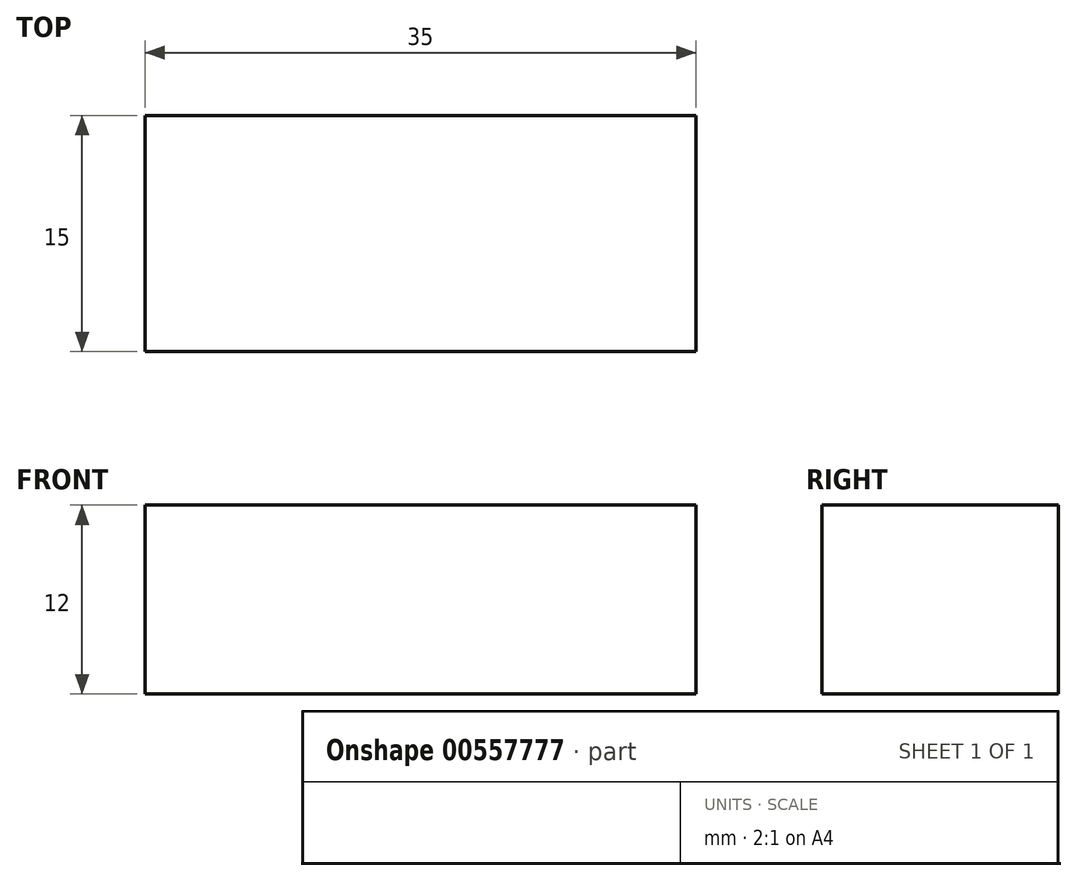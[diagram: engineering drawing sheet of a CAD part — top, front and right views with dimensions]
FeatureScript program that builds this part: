
annotation { "Feature Type Name" : "Feature", "Feature Type Description" : "" }
export const myFeature = defineFeature(function(context is Context, id is Id, definition is map)
    precondition{}
    {
        {
            var Q0;
            Q0=qCreatedBy(makeId("Top.planeOp"),FACE);
            var sketch = newSketch(context, id + "F0", { "sketchPlane" : qUnion([Q0])});
            skLineSegment(sketch, "E0.bottom", {"start": v(0, 0) * mm, "end": v(35, 0) * mm});
            skLineSegment(sketch, "E0.top", {"start": v(0, 15) * mm, "end": v(35, 15) * mm});
            skLineSegment(sketch, "E0.left", {"start": v(0, 0) * mm, "end": v(0, 15) * mm});
            skLineSegment(sketch, "E0.right", {"start": v(35, 0) * mm, "end": v(35, 15) * mm});
            skLineSegment(sketch, "E1", {"start": v(0, 7.5) * mm, "end": v(35, 7.5) * mm, "construction": true});
            skLineSegment(sketch, "E2", {"start": v(7.5, 15) * mm, "end": v(7.5, 0) * mm, "construction": true});
            skSolve(sketch);
        }
        {
            var Q0;
            Q0=makeQuery(id+"F0.imprint","IMPRINT",FACE,{"disambiguationData":[TD([[makeQuery(id+"F0.imprint","IMPRINT",EDGE,{"derivedFrom":sQuery(id+"F0.wireOp",EDGE,"E0.bottom")}),1.0]])]});
            extrude(context, id + "F1", {"entities" : qUnion([Q0]), "depth" : 12 * mm, "offsetDistance" : 25 * mm});
        }
    });
